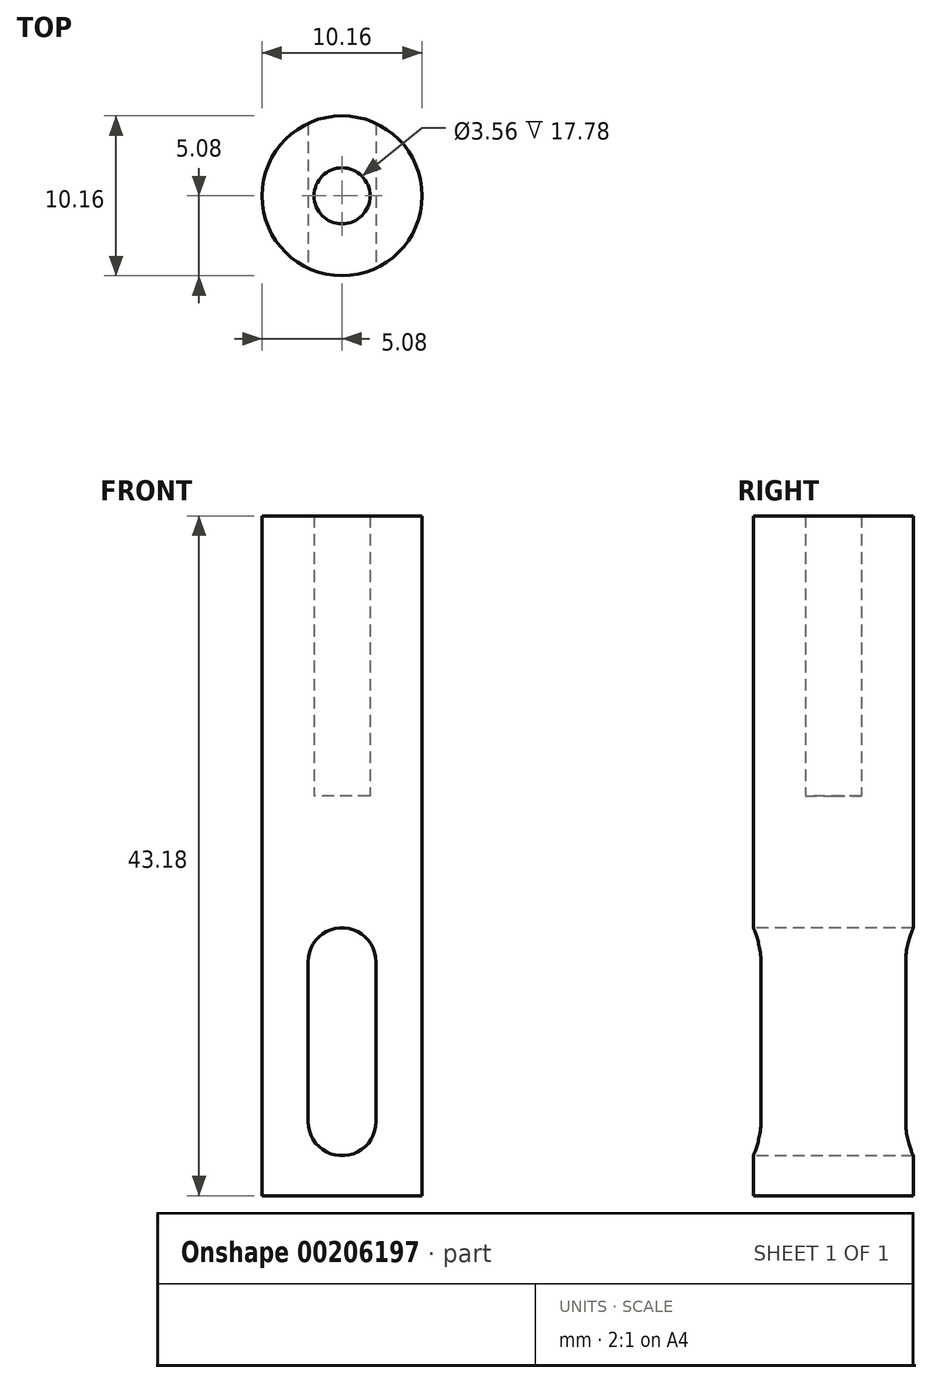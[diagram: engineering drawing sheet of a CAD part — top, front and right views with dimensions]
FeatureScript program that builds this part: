
annotation { "Feature Type Name" : "Feature", "Feature Type Description" : "" }
export const myFeature = defineFeature(function(context is Context, id is Id, definition is map)
    precondition{}
    {
        {
            var Q0;
            Q0=qCreatedBy(makeId("Top.planeOp"),FACE);
            var sketch = newSketch(context, id + "F0", { "sketchPlane" : qUnion([Q0])});
            skCircle(sketch, "E0", {"center": v(0, 0) * mm, "radius": 1.78 * mm});
            skCircle(sketch, "E1", {"center": v(0, 0) * mm, "radius": 5.08 * mm});
            skSolve(sketch);
        }
        {
            var Q0;
            Q0 = qSketchRegion(id + "F0", true);
            var Q1;
            Q1=makeQuery(id+"F0.imprint","IMPRINT",FACE,{"disambiguationData":[TD([[makeQuery(id+"F0.imprint","IMPRINT",EDGE,{"derivedFrom":sQuery(id+"F0.wireOp",EDGE,"E0")}),1.0]])]});
            extrude(context, id + "F1", {"entities" : qUnion([Q0, Q1]), "depth" : 25.4 * mm});
        }
        {
            var Q0;
            Q0=makeQuery(id+"F0.imprint","IMPRINT",FACE,{"disambiguationData":[TD([[makeQuery(id+"F0.imprint","IMPRINT",EDGE,{"derivedFrom":sQuery(id+"F0.wireOp",EDGE,"E0")}),-1.0]])]});
            extrude(context, id + "F2", {"entities" : qUnion([Q0]), "operationType" : NewBodyOperationType.ADD, "depth" : 43.18 * mm});
        }
        {
            var Q0;
            Q0=qCreatedBy(makeId("Front.planeOp"),FACE);
            var sketch = newSketch(context, id + "F3", { "sketchPlane" : qUnion([Q0])});
            skCircle(sketch, "E2", {"center": v(0, 4.7) * mm, "radius": 2.16 * mm});
            skCircle(sketch, "E3", {"center": v(0, 14.86) * mm, "radius": 2.16 * mm});
            skLineSegment(sketch, "E4", {"start": v(2.16, 14.86) * mm, "end": v(2.16, 4.7) * mm});
            skLineSegment(sketch, "E5", {"start": v(-2.16, 14.86) * mm, "end": v(-2.16, 4.7) * mm});
            skSolve(sketch);
        }
        {
            var Q0;
            Q0 = qSketchRegion(id + "F3", true);
            extrude(context, id + "F4", {"entities" : qUnion([Q0]), "operationType" : NewBodyOperationType.REMOVE, "oppositeDirection" : true, "depth" : 25.4 * mm, "hasSecondDirection" : true, "secondDirectionOppositeDirection" : false, "secondDirectionDepth" : 25.4 * mm});
        }
    });
